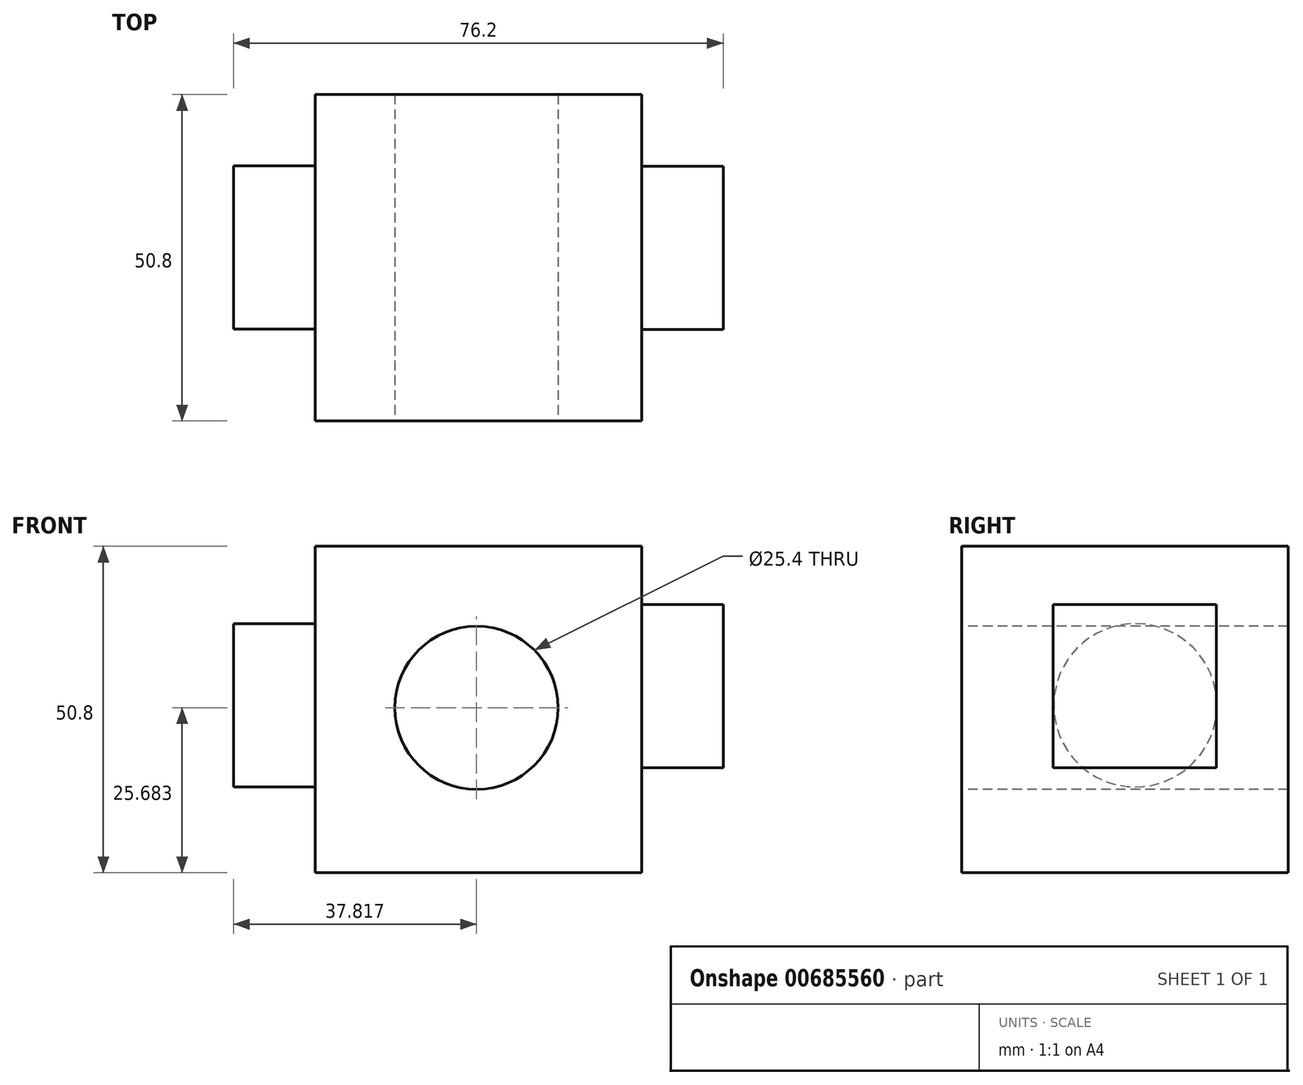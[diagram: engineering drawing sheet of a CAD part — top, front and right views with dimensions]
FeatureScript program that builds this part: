
annotation { "Feature Type Name" : "Feature", "Feature Type Description" : "" }
export const myFeature = defineFeature(function(context is Context, id is Id, definition is map)
    precondition{}
    {
        {
            var Q0;
            Q0=qCreatedBy(makeId("Front.planeOp"),FACE);
            var sketch = newSketch(context, id + "F0", { "sketchPlane" : qUnion([Q0])});
            skLineSegment(sketch, "E0", {"start": v(0, 0) * mm, "end": v(0, 50.8) * mm});
            skLineSegment(sketch, "E1", {"start": v(0, 50.8) * mm, "end": v(-50.8, 50.8) * mm});
            skLineSegment(sketch, "E2", {"start": v(-50.8, 50.8) * mm, "end": v(-50.8, 0) * mm});
            skLineSegment(sketch, "E3", {"start": v(-50.8, 0) * mm, "end": v(0, 0) * mm});
            skSolve(sketch);
        }
        {
            var Q0;
            Q0=makeQuery(id+"F0.imprint","IMPRINT",FACE,{"disambiguationData":[TD([[makeQuery(id+"F0.imprint","IMPRINT",EDGE,{"derivedFrom":sQuery(id+"F0.wireOp",EDGE,"E0")}),1.0]])]});
            extrude(context, id + "F1", {"entities" : qUnion([Q0]), "depth" : 50.8 * mm, "offsetDistance" : 25.4 * mm});
        }
        {
            var Q0;
            Q0=makeQuery(id+"F1.opExtrude","CAP_FACE",FACE,{"disambiguationData":[OSD([sQuery(id+"F0.wireOp",EDGE,"E0"),sQuery(id+"F0.wireOp",EDGE,"E1"),sQuery(id+"F0.wireOp",EDGE,"E2"),sQuery(id+"F0.wireOp",EDGE,"E3")])],"isStart":false});
            var sketch = newSketch(context, id + "F2", { "sketchPlane" : qUnion([Q0])});
            skCircle(sketch, "E4", {"center": v(-25.68, 25.68) * mm, "radius": 12.7 * mm});
            skSolve(sketch);
        }
        {
            var Q0;
            Q0 = qSketchRegion(id + "F2", true);
            extrude(context, id + "F3", {"entities" : qUnion([Q0]), "operationType" : NewBodyOperationType.REMOVE, "oppositeDirection" : true, "depth" : 50.8 * mm, "offsetDistance" : 25.4 * mm});
        }
        {
            var Q0;
            Q0=makeQuery(id+"F1.opExtrude","SWEPT_FACE",FACE,{"disambiguationData":[OSD([sQuery(id+"F0.wireOp",EDGE,"E2")])]});
            var sketch = newSketch(context, id + "F4", { "sketchPlane" : qUnion([Q0])});
            skCircle(sketch, "E5", {"center": v(23.77, 26.07) * mm, "radius": 12.7 * mm});
            skSolve(sketch);
        }
        {
            var Q0;
            Q0 = qSketchRegion(id + "F4", true);
            extrude(context, id + "F5", {"entities" : qUnion([Q0]), "operationType" : NewBodyOperationType.ADD, "depth" : 12.7 * mm, "offsetDistance" : 25.4 * mm});
        }
        {
            var Q0;
            Q0=makeQuery(id+"F1.opExtrude","SWEPT_FACE",FACE,{"disambiguationData":[OSD([sQuery(id+"F0.wireOp",EDGE,"E0")])]});
            var sketch = newSketch(context, id + "F6", { "sketchPlane" : qUnion([Q0])});
            skLineSegment(sketch, "E6.bottom", {"start": v(-36.57, 41.73) * mm, "end": v(-11.17, 41.73) * mm});
            skLineSegment(sketch, "E6.top", {"start": v(-36.57, 16.33) * mm, "end": v(-11.17, 16.33) * mm});
            skLineSegment(sketch, "E6.left", {"start": v(-36.57, 41.73) * mm, "end": v(-36.57, 16.33) * mm});
            skLineSegment(sketch, "E6.right", {"start": v(-11.17, 41.73) * mm, "end": v(-11.17, 16.33) * mm});
            skSolve(sketch);
        }
        {
            var Q0;
            Q0 = qSketchRegion(id + "F6", true);
            extrude(context, id + "F7", {"entities" : qUnion([Q0]), "operationType" : NewBodyOperationType.ADD, "depth" : 12.7 * mm, "offsetDistance" : 25.4 * mm});
        }
    });
